# Revit family: Турникет RTD-16
name_source: partatom
category: Обобщенные модели
units: mm (PartAtom-declared; Revit-internal decimal feet)

## family parameters
Всегда вертикально = Да
Может служить основой для арматурных стержней = Нет
На основе рабочей плоскости = Нет
Общий = Нет
При загрузке вырезать с полостями = Нет
Размер круглого соединителя = Использовать диаметр
Тип детали = Нормальный
Точка расчета площади = Нет

## types (4) — shared parameters
ADSK_URL страницы изделия = https://www.perco.ru
ADSK_Единица измерения = компл.
ADSK_Завод-изготовитель = PERCo
ADSK_Количество = 1
ADSK_Масса_Текст = от 191 кг
ADSK_Напряжение = 24В
ADSK_Номинальная мощность = 105Вт
ADSK_Ток = 4.5А
Габаритыне размеры (длина х ширина х высота) = 1595×1641×2303 мм
Материал турникета = Сталь окрашенная RAL 5010
Подключение к электросети = 220 В
Пропускная способность = 30 чел./мин
Степень защиты оболочки = IP54
Температура использования = от -40°C до +55°C
Ширина зоны прохода = 630 мм
zero-valued in all types: Отметка по умолчанию

## per-type parameters (varying)
| type | ADSK_Материал наименование | ADSK_Наименование | ADSK_Наименование краткое | Материал ротора |
| RTD-16.1 моторизированный | "Корпус и ротор - Сталь, обработанная 
методом горячего цинкования и покрытая порошковой краской." | Полноростовый роторный моторизированный турникет PERCo-RTD-16 | Турникет роторный моторизированный RTD-16.1 | Сталь, окрашенная, белая |
| RTD-16.1S моторизированный | "Корпус - сталь, обработанная 
методом горячего цинкования и покрытая порошковой краской. 
Ротор - нержавеющая сталь" | Полноростовый роторный моторизированный 
турникет PERCo-RTD-16 | Турникет роторный моторизированный RTD-16.1 | Сталь, нержавеющая AISI 304 |
| RTD-16.2S электромеханический | "Корпус - сталь, обработанная 
методом горячего цинкования и покрытая порошковой краской. 
Ротор - нержавеющая сталь" | Полноростовый роторный  электромеханический турникет PERCo-RTD-16 | Турникет роторный электромеханический RTD-16.1 | Сталь, нержавеющая AISI 304 |
| RTD-16.2 электромеханический | "Корпус - сталь, обработанная 
методом горячего цинкования и покрытая порошковой краской. 
Ротор - нержавеющая сталь" | Полноростовый роторный  электромеханический турникет PERCo-RTD-16 | Турникет роторный электромеханический RTD-16.1 | Сталь, окрашенная, белая |
